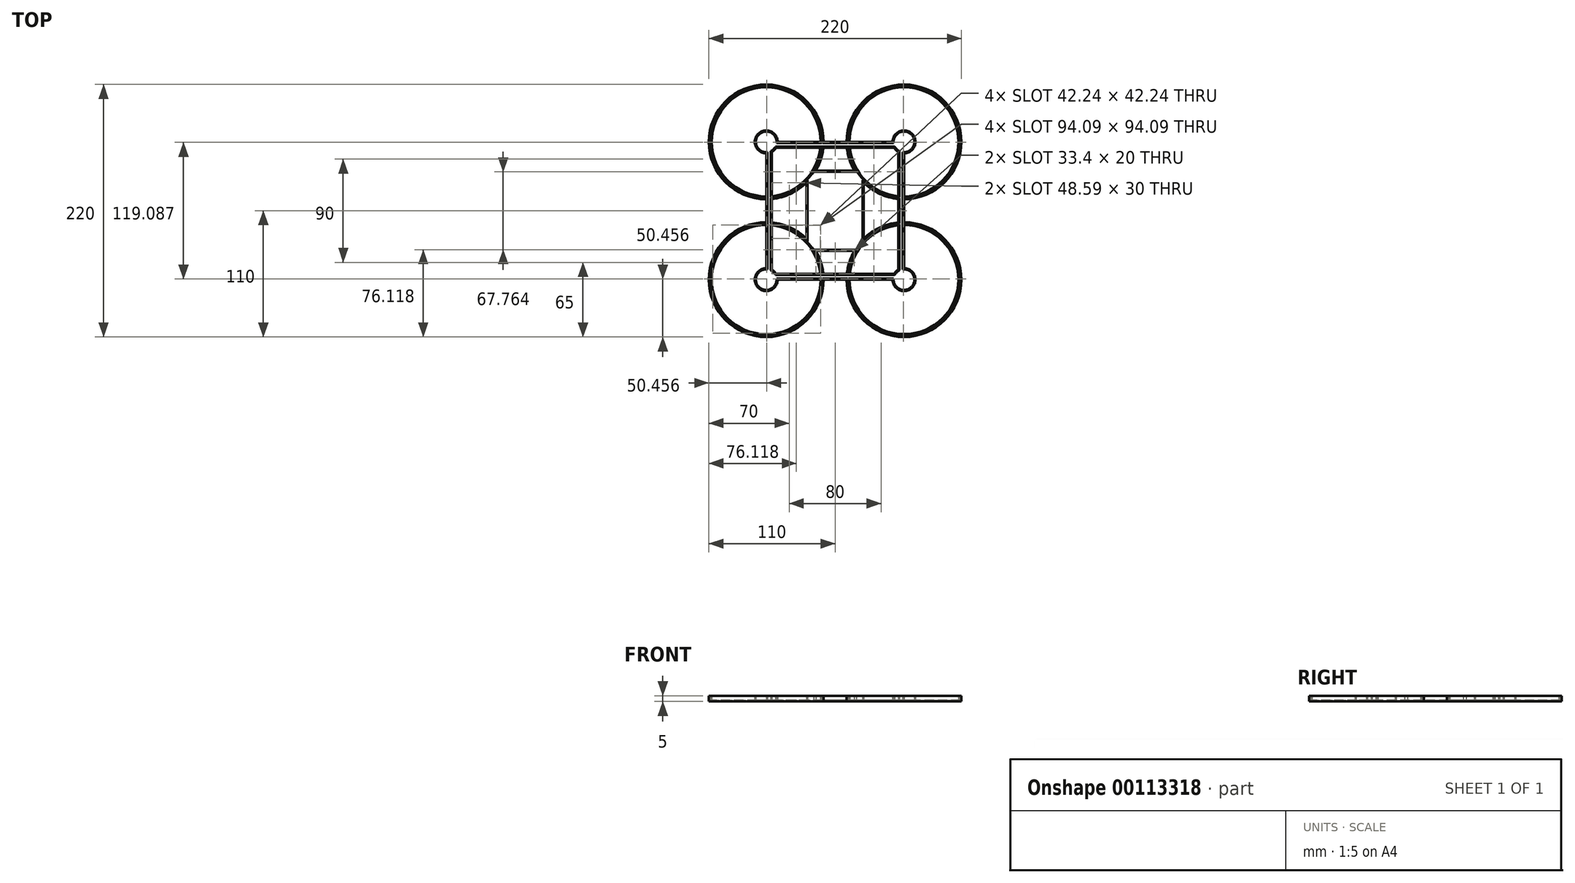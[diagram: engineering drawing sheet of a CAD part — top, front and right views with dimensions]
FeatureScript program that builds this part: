
annotation { "Feature Type Name" : "Feature", "Feature Type Description" : "" }
export const myFeature = defineFeature(function(context is Context, id is Id, definition is map)
    precondition{}
    {
        {
            var Q0;
            Q0=qCreatedBy(makeId("Top.planeOp"),FACE);
            var sketch = newSketch(context, id + "F0", { "sketchPlane" : qUnion([Q0])});
            skLineSegment(sketch, "E0.bottom", {"start": v(50, 60) * mm, "end": v(12.5, 60) * mm});
            skLineSegment(sketch, "E0.top", {"start": v(50, -60) * mm, "end": v(12.5, -60) * mm});
            skLineSegment(sketch, "E0.left", {"start": v(60, 50) * mm, "end": v(60, 12.5) * mm});
            skLineSegment(sketch, "E0.right", {"start": v(-60, 50) * mm, "end": v(-60, 12.5) * mm});
            skPoint(sketch, "E0.middle", {"position": v(0, 0) * mm});
            skArc(sketch, "E1", {"start": v(-16.7, 35) * mm, "mid": v(-12.41, 44.66) * mm, "end": v(-10.25, 55) * mm});
            skArc(sketch, "E2", {"start": v(-25, -24.3) * mm, "mid": v(-38.8, -14.72) * mm, "end": v(-55, -10.25) * mm});
            skArc(sketch, "E3", {"start": v(55, -10.25) * mm, "mid": v(38.8, -14.72) * mm, "end": v(25, -24.3) * mm});
            skArc(sketch, "E4", {"start": v(10.25, 55) * mm, "mid": v(12.41, 44.66) * mm, "end": v(16.7, 35) * mm});
            skArc(sketch, "E5", {"start": v(-55, 12.76) * mm, "mid": v(-26.41, 26.41) * mm, "end": v(-12.76, 55) * mm});
            skArc(sketch, "E6", {"start": v(-12.76, -55) * mm, "mid": v(-26.41, -26.41) * mm, "end": v(-55, -12.76) * mm});
            skArc(sketch, "E7", {"start": v(55, -12.76) * mm, "mid": v(26.41, -26.41) * mm, "end": v(12.76, -55) * mm});
            skArc(sketch, "E8", {"start": v(12.76, 55) * mm, "mid": v(26.41, 26.41) * mm, "end": v(55, 12.76) * mm});
            skLineSegment(sketch, "E9.bottom", {"start": v(16.7, -35) * mm, "end": v(-16.7, -35) * mm});
            skLineSegment(sketch, "E9.top", {"start": v(16.7, 35) * mm, "end": v(-16.7, 35) * mm});
            skLineSegment(sketch, "E9.left", {"start": v(25, -24.3) * mm, "end": v(25, 24.3) * mm});
            skLineSegment(sketch, "E9.right", {"start": v(-25, -24.3) * mm, "end": v(-25, 24.3) * mm});
            skLineSegment(sketch, "E10.bottom", {"start": v(-51.34, 55) * mm, "end": v(-12.76, 55) * mm});
            skLineSegment(sketch, "E10.top", {"start": v(-51.34, -55) * mm, "end": v(-12.76, -55) * mm});
            skLineSegment(sketch, "E10.left", {"start": v(-55, 51.34) * mm, "end": v(-55, 12.76) * mm});
            skLineSegment(sketch, "E10.right", {"start": v(55, 51.34) * mm, "end": v(55, 12.76) * mm});
            skArc(sketch, "E11", {"start": v(-50, 60) * mm, "mid": v(-67.07, 67.07) * mm, "end": v(-60, 50) * mm});
            skArc(sketch, "E12", {"start": v(51.34, 55) * mm, "mid": v(52.93, 52.93) * mm, "end": v(55, 51.34) * mm});
            skArc(sketch, "E13", {"start": v(55, -51.34) * mm, "mid": v(52.93, -52.93) * mm, "end": v(51.34, -55) * mm});
            skArc(sketch, "E14", {"start": v(-51.34, -55) * mm, "mid": v(-52.93, -52.93) * mm, "end": v(-55, -51.34) * mm});
            skPoint(sketch, "E15.orphan", {"position": v(-55, 55) * mm});
            skPoint(sketch, "E16.orphan", {"position": v(-25, 35) * mm});
            skArc(sketch, "E17.trimOffspring", {"start": v(-55, 10.25) * mm, "mid": v(-38.8, 14.72) * mm, "end": v(-25, 24.3) * mm});
            skLineSegment(sketch, "E18.trimOffspring", {"start": v(-55, 10.25) * mm, "end": v(-55, -10.25) * mm});
            skLineSegment(sketch, "E19.trimOffspring", {"start": v(-60, 10) * mm, "end": v(-60, -10) * mm});
            skArc(sketch, "E20.trimOffspring", {"start": v(-55, 51.34) * mm, "mid": v(-52.93, 52.93) * mm, "end": v(-51.34, 55) * mm});
            skArc(sketch, "E21.trimOffspring", {"start": v(-12.5, 60) * mm, "mid": v(-93.59, 93.59) * mm, "end": v(-60, 12.5) * mm});
            skArc(sketch, "E22.trimOffspring", {"start": v(-10, 60) * mm, "mid": v(-95.36, 95.36) * mm, "end": v(-60, 10) * mm});
            skLineSegment(sketch, "E23.trimOffspring", {"start": v(-12.5, 60) * mm, "end": v(-50, 60) * mm});
            skLineSegment(sketch, "E24.trimOffspring", {"start": v(-10.25, 55) * mm, "end": v(10.25, 55) * mm});
            skLineSegment(sketch, "E25.trimOffspring", {"start": v(10, 60) * mm, "end": v(-10, 60) * mm});
            skLineSegment(sketch, "E26.trimOffspring", {"start": v(12.76, 55) * mm, "end": v(51.34, 55) * mm});
            skPoint(sketch, "E27.orphan", {"position": v(55, 55) * mm});
            skArc(sketch, "E28.trimOffspring", {"start": v(60, 50) * mm, "mid": v(67.07, 67.07) * mm, "end": v(50, 60) * mm});
            skPoint(sketch, "E29.orphan", {"position": v(25, 35) * mm});
            skArc(sketch, "E30.trimOffspring", {"start": v(60, 12.5) * mm, "mid": v(93.59, 93.59) * mm, "end": v(12.5, 60) * mm});
            skArc(sketch, "E31.trimOffspring", {"start": v(60, 10) * mm, "mid": v(95.36, 95.36) * mm, "end": v(10, 60) * mm});
            skLineSegment(sketch, "E32.trimOffspring", {"start": v(55, 10.25) * mm, "end": v(55, -10.25) * mm});
            skLineSegment(sketch, "E33.trimOffspring", {"start": v(60, 10) * mm, "end": v(60, -10) * mm});
            skLineSegment(sketch, "E34.trimOffspring", {"start": v(55, -12.76) * mm, "end": v(55, -51.34) * mm});
            skLineSegment(sketch, "E35.trimOffspring", {"start": v(60, -12.5) * mm, "end": v(60, -50) * mm});
            skPoint(sketch, "E36.orphan", {"position": v(55, -55) * mm});
            skArc(sketch, "E37.trimOffspring", {"start": v(50, -60) * mm, "mid": v(67.07, -67.07) * mm, "end": v(60, -50) * mm});
            skPoint(sketch, "E38.orphan", {"position": v(25, -35) * mm});
            skArc(sketch, "E39.trimOffspring", {"start": v(16.7, -35) * mm, "mid": v(12.41, -44.66) * mm, "end": v(10.25, -55) * mm});
            skPoint(sketch, "E40.orphan", {"position": v(-25, -35) * mm});
            skArc(sketch, "E41.trimOffspring", {"start": v(25, 24.3) * mm, "mid": v(38.8, 14.72) * mm, "end": v(55, 10.25) * mm});
            skArc(sketch, "E42.trimOffspring", {"start": v(12.5, -60) * mm, "mid": v(93.59, -93.59) * mm, "end": v(60, -12.5) * mm});
            skLineSegment(sketch, "E43.trimOffspring", {"start": v(12.76, -55) * mm, "end": v(51.34, -55) * mm});
            skLineSegment(sketch, "E44.trimOffspring", {"start": v(10, -60) * mm, "end": v(-10, -60) * mm});
            skArc(sketch, "E45.trimOffspring", {"start": v(10, -60) * mm, "mid": v(95.36, -95.36) * mm, "end": v(60, -10) * mm});
            skArc(sketch, "E46.trimOffspring", {"start": v(-10.25, -55) * mm, "mid": v(-12.41, -44.66) * mm, "end": v(-16.7, -35) * mm});
            skLineSegment(sketch, "E47.trimOffspring", {"start": v(-10.25, -55) * mm, "end": v(10.25, -55) * mm});
            skLineSegment(sketch, "E48.trimOffspring", {"start": v(-12.5, -60) * mm, "end": v(-50, -60) * mm});
            skPoint(sketch, "E49.orphan", {"position": v(-55, -55) * mm});
            skArc(sketch, "E50.trimOffspring", {"start": v(-60, -50) * mm, "mid": v(-67.07, -67.07) * mm, "end": v(-50, -60) * mm});
            skArc(sketch, "E51.trimOffspring", {"start": v(-60, -12.5) * mm, "mid": v(-93.59, -93.59) * mm, "end": v(-12.5, -60) * mm});
            skArc(sketch, "E52.trimOffspring", {"start": v(-60, -10) * mm, "mid": v(-95.36, -95.36) * mm, "end": v(-10, -60) * mm});
            skLineSegment(sketch, "E53.trimOffspring", {"start": v(-60, -12.5) * mm, "end": v(-60, -50) * mm});
            skLineSegment(sketch, "E54.trimOffspring", {"start": v(-55, -12.76) * mm, "end": v(-55, -51.34) * mm});
            skSolve(sketch);
        }
        {
            var Q0;
            Q0 = qSketchRegion(id + "F0", true);
            var Q1;
            Q1=makeQuery(id+"F0.imprint","IMPRINT",FACE,{"disambiguationData":[TD([[makeQuery(id+"F0.imprint","IMPRINT",EDGE,{"derivedFrom":sQuery(id+"F0.wireOp",EDGE,"E0.bottom")}),1.0]])]});
            extrude(context, id + "F1", {"entities" : qUnion([Q0, Q1]), "depth" : 5 * mm});
        }
        {
            var Q0;
            Q0=makeQuery(id+"F1.opExtrude","CAP_FACE",FACE,{"disambiguationData":[OSD([sQuery(id+"F0.wireOp",EDGE,"E0.bottom"),sQuery(id+"F0.wireOp",EDGE,"E0.top"),sQuery(id+"F0.wireOp",EDGE,"E0.left"),sQuery(id+"F0.wireOp",EDGE,"E0.right"),sQuery(id+"F0.wireOp",EDGE,"E1"),sQuery(id+"F0.wireOp",EDGE,"E2"),sQuery(id+"F0.wireOp",EDGE,"E3"),sQuery(id+"F0.wireOp",EDGE,"E4"),sQuery(id+"F0.wireOp",EDGE,"E5"),sQuery(id+"F0.wireOp",EDGE,"E6"),sQuery(id+"F0.wireOp",EDGE,"E7"),sQuery(id+"F0.wireOp",EDGE,"E8"),sQuery(id+"F0.wireOp",EDGE,"E9.bottom"),sQuery(id+"F0.wireOp",EDGE,"E9.top"),sQuery(id+"F0.wireOp",EDGE,"E9.left"),sQuery(id+"F0.wireOp",EDGE,"E9.right"),sQuery(id+"F0.wireOp",EDGE,"E10.bottom"),sQuery(id+"F0.wireOp",EDGE,"E10.top"),sQuery(id+"F0.wireOp",EDGE,"E10.left"),sQuery(id+"F0.wireOp",EDGE,"E10.right"),sQuery(id+"F0.wireOp",EDGE,"E11"),sQuery(id+"F0.wireOp",EDGE,"E12"),sQuery(id+"F0.wireOp",EDGE,"E13"),sQuery(id+"F0.wireOp",EDGE,"E14"),sQuery(id+"F0.wireOp",EDGE,"E17.trimOffspring"),sQuery(id+"F0.wireOp",EDGE,"E18.trimOffspring"),sQuery(id+"F0.wireOp",EDGE,"E19.trimOffspring"),sQuery(id+"F0.wireOp",EDGE,"E20.trimOffspring"),sQuery(id+"F0.wireOp",EDGE,"E21.trimOffspring"),sQuery(id+"F0.wireOp",EDGE,"E22.trimOffspring"),sQuery(id+"F0.wireOp",EDGE,"E23.trimOffspring"),sQuery(id+"F0.wireOp",EDGE,"E24.trimOffspring"),sQuery(id+"F0.wireOp",EDGE,"E25.trimOffspring"),sQuery(id+"F0.wireOp",EDGE,"E26.trimOffspring"),sQuery(id+"F0.wireOp",EDGE,"E28.trimOffspring"),sQuery(id+"F0.wireOp",EDGE,"E30.trimOffspring"),sQuery(id+"F0.wireOp",EDGE,"E31.trimOffspring"),sQuery(id+"F0.wireOp",EDGE,"E32.trimOffspring"),sQuery(id+"F0.wireOp",EDGE,"E33.trimOffspring"),sQuery(id+"F0.wireOp",EDGE,"E34.trimOffspring"),sQuery(id+"F0.wireOp",EDGE,"E35.trimOffspring"),sQuery(id+"F0.wireOp",EDGE,"E37.trimOffspring"),sQuery(id+"F0.wireOp",EDGE,"E39.trimOffspring"),sQuery(id+"F0.wireOp",EDGE,"E41.trimOffspring"),sQuery(id+"F0.wireOp",EDGE,"E42.trimOffspring"),sQuery(id+"F0.wireOp",EDGE,"E43.trimOffspring"),sQuery(id+"F0.wireOp",EDGE,"E44.trimOffspring"),sQuery(id+"F0.wireOp",EDGE,"E45.trimOffspring"),sQuery(id+"F0.wireOp",EDGE,"E46.trimOffspring"),sQuery(id+"F0.wireOp",EDGE,"E47.trimOffspring"),sQuery(id+"F0.wireOp",EDGE,"E48.trimOffspring"),sQuery(id+"F0.wireOp",EDGE,"E50.trimOffspring"),sQuery(id+"F0.wireOp",EDGE,"E51.trimOffspring"),sQuery(id+"F0.wireOp",EDGE,"E52.trimOffspring"),sQuery(id+"F0.wireOp",EDGE,"E53.trimOffspring"),sQuery(id+"F0.wireOp",EDGE,"E54.trimOffspring")])],"isStart":false});
            shell(context, id + "F2", {"entities" : qUnion([Q0]), "thickness" : 1 * mm});
        }
    });
